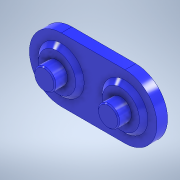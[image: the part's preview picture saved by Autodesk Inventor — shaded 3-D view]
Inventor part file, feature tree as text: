
AUTODESK INVENTOR PART (.ipt)
format: ipt  version: 2022 (Build 260153000, 153)  size: 149,504 bytes
history: native  units: mm
features: extrude x3, chamfer x2, other x1, sketch x1
ambient origin geometry x8: Origin, YZ Plane, XZ Plane, XY Plane, X Axis, Y Axis, Z Axis, Center Point
bodies: Body1 (feature_tree)
feature tree (7):
  other  "Sólido1"
  sketch  "Esboço1"  dims[d0=60.0mm d1=60.0mm d2=30.0mm d3=35.0mm d4=20.0mm d5=10.0mm d6=0.0mm d7=14.0mm d8=0.0mm d9=26.0mm d10=0.0mm d11=35.0mm d12=20.0mm d13=4.0mm d14=2.0mm d15=45.0deg d16=1.0mm d17=2.0mm d18=45.0deg]
  extrude  "Extrusão1"  Depth=60.0mm
  extrude  "Extrusão2"  Depth=30.0mm
  extrude  "Extrusão3"  Depth=4.0mm
  chamfer  "Chanfro1"  Distance=20.0mm
  chamfer  "Chanfro2"  Distance=10.0mm
